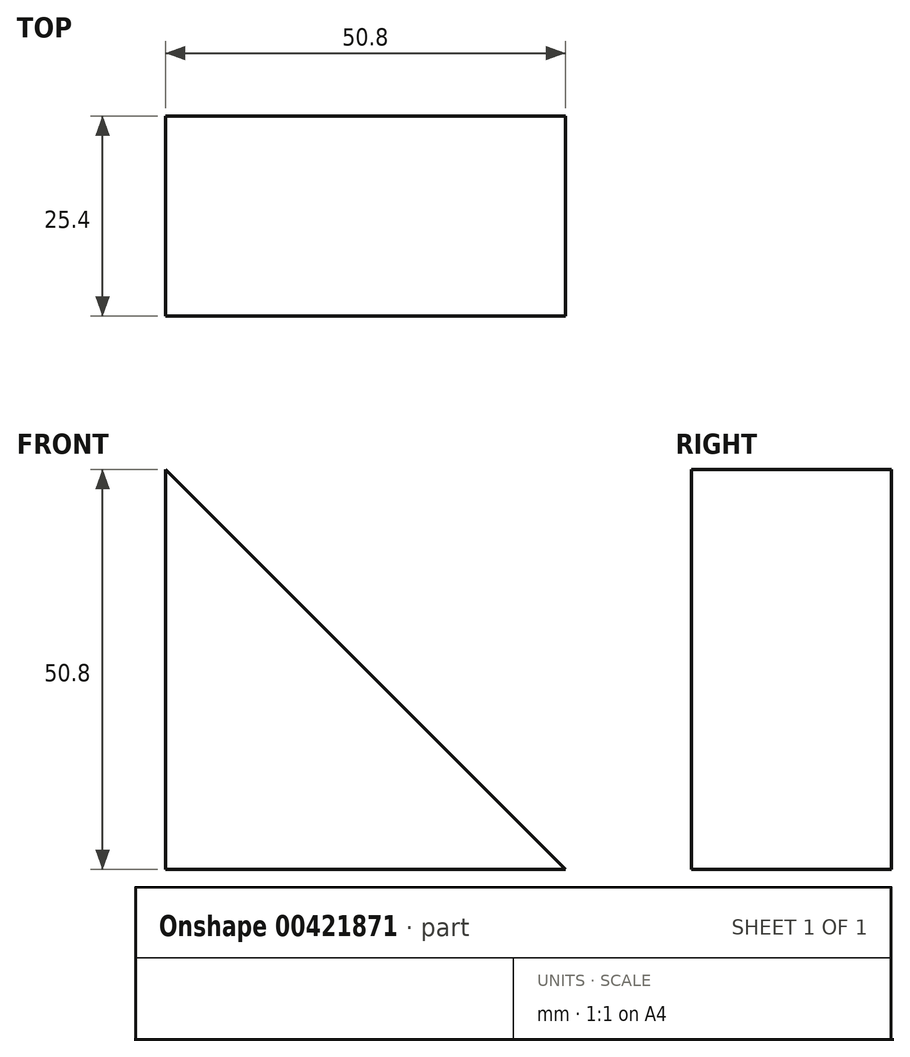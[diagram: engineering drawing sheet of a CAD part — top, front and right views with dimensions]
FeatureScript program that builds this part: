
annotation { "Feature Type Name" : "Feature", "Feature Type Description" : "" }
export const myFeature = defineFeature(function(context is Context, id is Id, definition is map)
    precondition{}
    {
        {
            var Q0;
            Q0=qCreatedBy(makeId("Front.planeOp"),FACE);
            var sketch = newSketch(context, id + "F0", { "sketchPlane" : qUnion([Q0])});
            skLineSegment(sketch, "E0", {"start": v(-50.8, 0) * mm, "end": v(-50.8, 50.8) * mm});
            skLineSegment(sketch, "E1", {"start": v(-50.8, 0) * mm, "end": v(0, 0) * mm});
            skLineSegment(sketch, "E2", {"start": v(-50.8, 50.8) * mm, "end": v(0, 0) * mm});
            skSolve(sketch);
        }
        {
            var Q0;
            Q0=makeQuery(id+"F0.imprint","IMPRINT",FACE,{"disambiguationData":[TD([[makeQuery(id+"F0.imprint","IMPRINT",EDGE,{"derivedFrom":sQuery(id+"F0.wireOp",EDGE,"E0")}),-1.0]])]});
            extrude(context, id + "F1", {"entities" : qUnion([Q0]), "depth" : 25.4 * mm});
        }
    });
